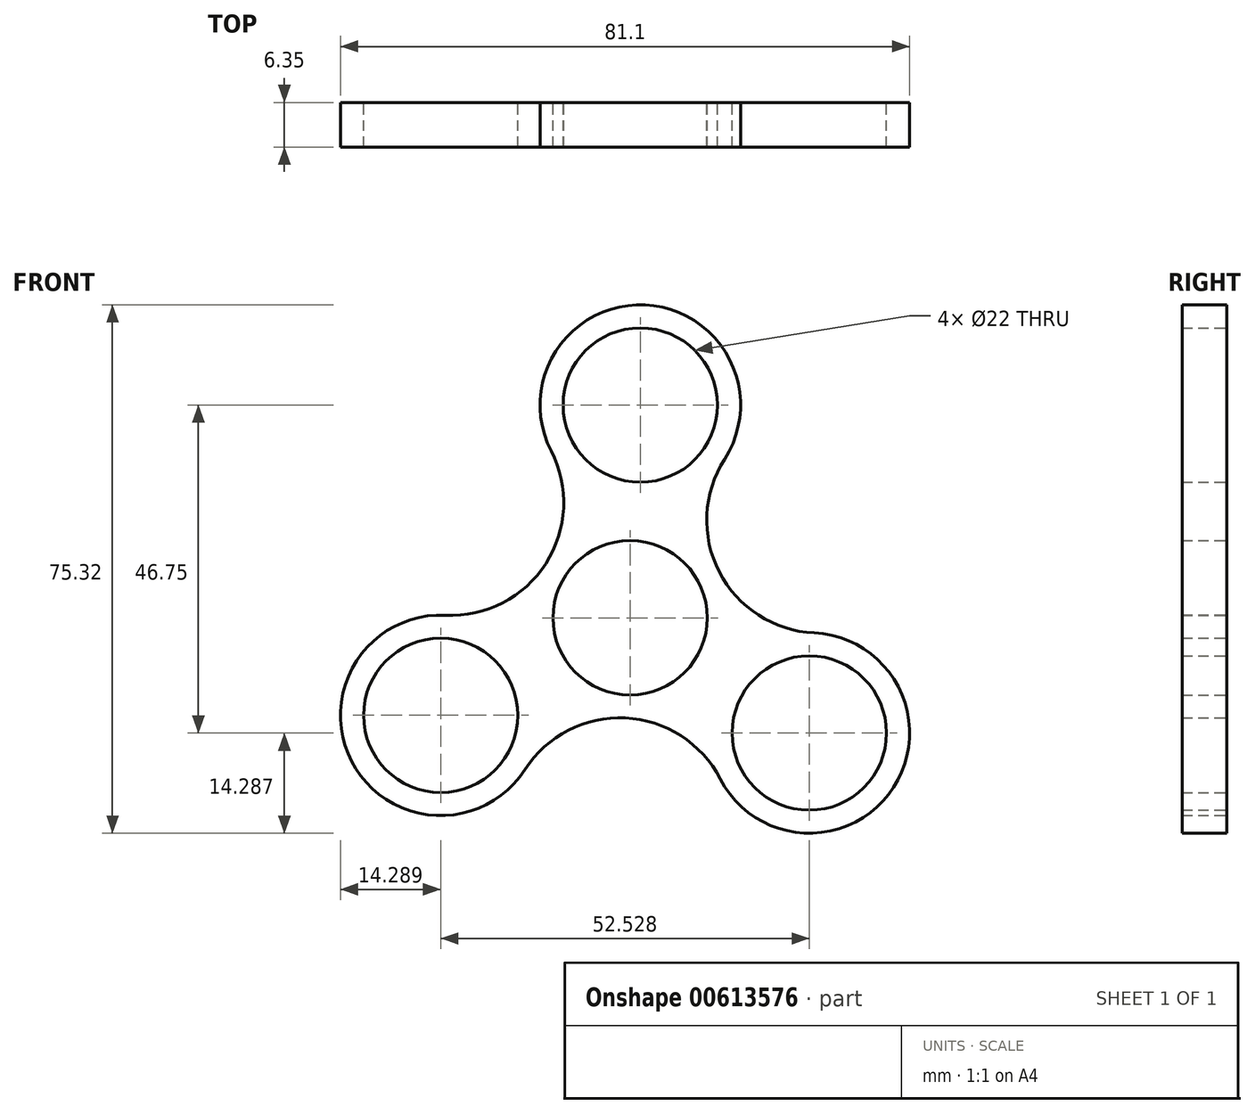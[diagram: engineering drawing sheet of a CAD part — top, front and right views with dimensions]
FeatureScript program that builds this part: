
annotation { "Feature Type Name" : "Feature", "Feature Type Description" : "" }
export const myFeature = defineFeature(function(context is Context, id is Id, definition is map)
    precondition{}
    {
        {
            var Q0;
            Q0=qCreatedBy(makeId("Front.planeOp"),FACE);
            var sketch = newSketch(context, id + "F0", { "sketchPlane" : qUnion([Q0])});
            skCircle(sketch, "E0", {"center": v(0, 0) * mm, "radius": 14.29 * mm});
            skCircle(sketch, "E1", {"center": v(0, 0) * mm, "radius": 11 * mm});
            skCircle(sketch, "E2", {"center": v(25.54, -16.42) * mm, "radius": 14.29 * mm});
            skCircle(sketch, "E3", {"center": v(25.54, -16.42) * mm, "radius": 11 * mm});
            skCircle(sketch, "E4.1.2", {"center": v(1.45, 30.33) * mm, "radius": 14.29 * mm});
            skCircle(sketch, "E4.1.3", {"center": v(1.45, 30.33) * mm, "radius": 11 * mm});
            skCircle(sketch, "E4.2.2", {"center": v(-27, -13.9) * mm, "radius": 14.29 * mm});
            skCircle(sketch, "E4.2.3", {"center": v(-27, -13.9) * mm, "radius": 11 * mm});
            skArc(sketch, "E5", {"start": v(13.47, 22.6) * mm, "mid": v(12.7, 6.54) * mm, "end": v(26.22, -2.15) * mm});
            skArc(sketch, "E6", {"start": v(-26.3, 0.37) * mm, "mid": v(-12.02, 7.73) * mm, "end": v(-11.25, 23.78) * mm});
            skArc(sketch, "E7", {"start": v(12.84, -22.97) * mm, "mid": v(-0.68, -14.27) * mm, "end": v(-14.97, -21.63) * mm});
            skSolve(sketch);
        }
        {
            var Q0;
            {var subQ0=sQuery(id+"F0.wireOp",EDGE,"E5");var subQ1=sQuery(id+"F0.wireOp",EDGE,"E2");var subQ2=makeQuery(id+"F0.imprint","INTERSECT",VERTEX,{"derivedFrom":[subQ1,subQ0]});Q0=makeQuery(id+"F0.imprint","IMPRINT",FACE,{"disambiguationData":[TD([[makeQuery(id+"F0.imprint","IMPRINT",EDGE,{"disambiguationData":[TD([[subQ2,-1.0]])],"derivedFrom":subQ1}),-1.0]])]});}
            var Q1;
            {var subQ0=sQuery(id+"F0.wireOp",EDGE,"E7");var subQ1=sQuery(id+"F0.wireOp",EDGE,"E0");var subQ2=makeQuery(id+"F0.imprint","INTERSECT",VERTEX,{"derivedFrom":[subQ1,subQ0]});Q1=makeQuery(id+"F0.imprint","IMPRINT",FACE,{"disambiguationData":[TD([[makeQuery(id+"F0.imprint","IMPRINT",EDGE,{"disambiguationData":[TD([[subQ2,1.0]])],"derivedFrom":subQ1}),-1.0]])]});}
            var Q2;
            {var subQ0=sQuery(id+"F0.wireOp",EDGE,"E5");var subQ1=sQuery(id+"F0.wireOp",EDGE,"E4.1.2");var subQ2=makeQuery(id+"F0.imprint","INTERSECT",VERTEX,{"derivedFrom":[subQ1,subQ0]});Q2=makeQuery(id+"F0.imprint","IMPRINT",FACE,{"disambiguationData":[TD([[makeQuery(id+"F0.imprint","IMPRINT",EDGE,{"disambiguationData":[TD([[subQ2,1.0]])],"derivedFrom":subQ1}),-1.0]])]});}
            var Q3;
            Q3=makeQuery(id+"F0.imprint","IMPRINT",FACE,{"disambiguationData":[TD([[makeQuery(id+"F0.imprint","IMPRINT",EDGE,{"derivedFrom":sQuery(id+"F0.wireOp",EDGE,"E3")}),-1.0]])]});
            var Q4;
            Q4=makeQuery(id+"F0.imprint","IMPRINT",FACE,{"disambiguationData":[TD([[makeQuery(id+"F0.imprint","IMPRINT",EDGE,{"derivedFrom":sQuery(id+"F0.wireOp",EDGE,"E4.1.3")}),-1.0]])]});
            var Q5;
            Q5=makeQuery(id+"F0.imprint","IMPRINT",FACE,{"disambiguationData":[TD([[makeQuery(id+"F0.imprint","IMPRINT",EDGE,{"derivedFrom":sQuery(id+"F0.wireOp",EDGE,"E1")}),-1.0]])]});
            var Q6;
            Q6=makeQuery(id+"F0.imprint","IMPRINT",FACE,{"disambiguationData":[TD([[makeQuery(id+"F0.imprint","IMPRINT",EDGE,{"derivedFrom":sQuery(id+"F0.wireOp",EDGE,"E4.2.3")}),-1.0]])]});
            extrude(context, id + "F1", {"entities" : qUnion([Q0, Q1, Q2, Q3, Q4, Q5, Q6]), "depth" : 6.35 * mm, "offsetDistance" : 25.4 * mm});
        }
    });
